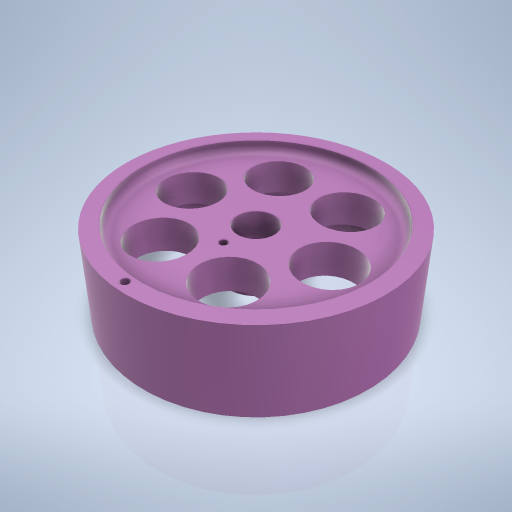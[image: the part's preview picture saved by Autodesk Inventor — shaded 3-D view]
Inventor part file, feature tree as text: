
AUTODESK INVENTOR PART (.ipt)
format: ipt  version: 2024.2 (Build 282272000, 272)  size: 350,208 bytes
history: native  units: mm
features: sketch x8, extrude x4, hole x4, fillet x2, pattern_circular x1
ambient origin geometry x8: Origin, YZ Plane, XZ Plane, XY Plane, X Axis, Y Axis, Z Axis, Center Point
bodies: Volumenkörper1 (feature_tree)
feature tree (19):
  extrude  "Extrusion1"  Depth=21.0mm TaperAngle=0.0deg
  extrude  "Extrusion2"  Depth=3.0mm TaperAngle=0.0deg
  fillet  "Rundung1"  Radius=2.0mm
  extrude  "Extrusion3"  Depth=10.0mm TaperAngle=0.0deg
  fillet  "Rundung2"  Radius=2.0mm
  extrude  "Extrusion4"  Depth=3.5mm TaperAngle=0.0deg
  hole  "Bohrung1"  [1 undecoded]
  hole  "Bohrung2"  [1 undecoded]
  pattern_circular  "Runde Anordnung1"  [2 undecoded]
  hole  "Bohrung3"  [1 undecoded]
  hole  "Bohrung4"  [1 undecoded]
  sketch  "Skizze1"  dims[d0=68.0mm d1=21.0mm d2=0.0mm]
  sketch  "Skizze2"  dims[d3=60.0mm d4=3.0mm d5=0.0mm d6=2.0mm]
  sketch  "Skizze3"  dims[d7=60.0mm d8=10.0mm d9=0.0mm d10=2.0mm]
  sketch  "Skizze4"  dims[d11=16.0mm d12=3.5mm d13=0.0mm]
  sketch  "Skizze5"  dims[d14=10.0mm d15=6.0mm d16=4.0mm d17=2.0mm d18=90.0deg d19=8.0mm d20=20.594885mm d21=30.0deg]
  sketch  "Skizze6"  dims[d22=38.0mm]
  sketch  "Skizze7"  dims[d23=15.0mm d24=6.0mm d25=4.0mm d26=2.0mm d27=90.0deg d28=8.0mm d29=0.0mm d30=60.0mm d31=360.0deg]
  sketch  "Skizze8"  dims[d33=2.0mm d34=6.0mm d35=4.0mm d36=2.0mm d37=90.0deg d38=8.0mm d39=0.0mm d40=31.75mm d41=2.0mm d42=6.0mm d43=4.0mm d44=2.0mm d45=90.0deg d46=8.0mm d47=0.0mm d48=8.75mm]
note: 6 required parameter values undecoded (feature->parameter linkage not recoverable at this tier; creation-order binding heuristic only, values carry confidence <= 0.55)
